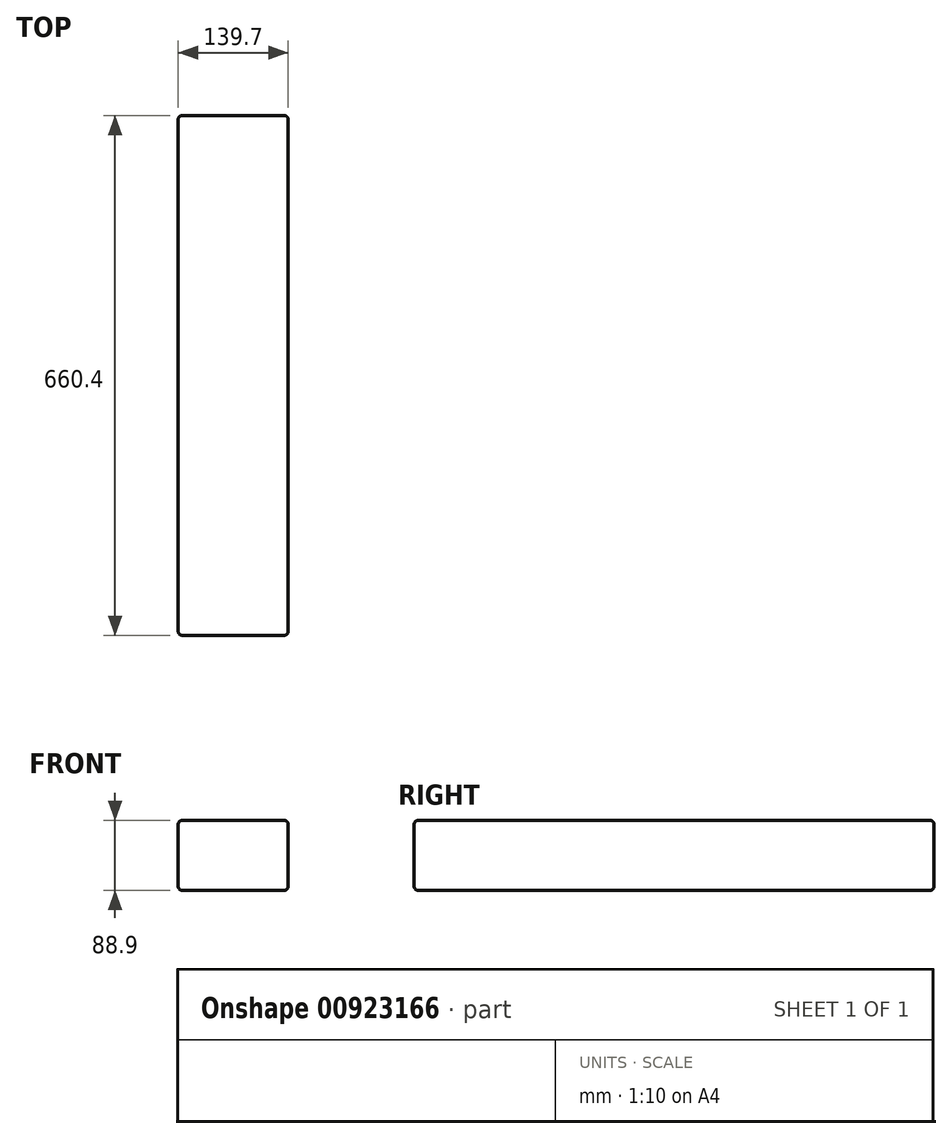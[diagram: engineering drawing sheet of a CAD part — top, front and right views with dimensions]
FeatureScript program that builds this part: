
annotation { "Feature Type Name" : "Feature", "Feature Type Description" : "" }
export const myFeature = defineFeature(function(context is Context, id is Id, definition is map)
    precondition{}
    {
        {
            var Q0;
            Q0=qCreatedBy(makeId("Front.planeOp"),FACE);
            var sketch = newSketch(context, id + "F0", { "sketchPlane" : qUnion([Q0])});
            skLineSegment(sketch, "E0.bottom", {"start": v(-69.85, 44.45) * mm, "end": v(69.85, 44.45) * mm});
            skLineSegment(sketch, "E0.top", {"start": v(-69.85, -44.45) * mm, "end": v(69.85, -44.45) * mm});
            skLineSegment(sketch, "E0.left", {"start": v(-69.85, 44.45) * mm, "end": v(-69.85, -44.45) * mm});
            skLineSegment(sketch, "E0.right", {"start": v(69.85, 44.45) * mm, "end": v(69.85, -44.45) * mm});
            skPoint(sketch, "E0.middle", {"position": v(0, 0) * mm});
            skSolve(sketch);
        }
        {
            var Q0;
            Q0=makeQuery(id+"F0.imprint","IMPRINT",FACE,{"disambiguationData":[TD([[makeQuery(id+"F0.imprint","IMPRINT",EDGE,{"derivedFrom":sQuery(id+"F0.wireOp",EDGE,"E0.bottom")}),-1.0]])]});
            extrude(context, id + "F1", {"entities" : qUnion([Q0]), "endBound" : BoundingType.SYMMETRIC, "depth" : 660.4 * mm, "offsetDistance" : 25.4 * mm});
        }
        {
            var Q0;
            Q0=makeQuery(id+"F1.opExtrude","CAP_EDGE",EDGE,{"disambiguationData":[OSD([sQuery(id+"F0.wireOp",EDGE,"E0.bottom")])],"isStart":false});
            var Q1;
            Q1=makeQuery(id+"F1.opExtrude","CAP_EDGE",EDGE,{"disambiguationData":[OSD([sQuery(id+"F0.wireOp",EDGE,"E0.left")])],"isStart":false});
            var Q2;
            Q2=makeQuery(id+"F1.opExtrude","CAP_EDGE",EDGE,{"disambiguationData":[OSD([sQuery(id+"F0.wireOp",EDGE,"E0.right")])],"isStart":false});
            var Q3;
            Q3=makeQuery(id+"F1.opExtrude","CAP_EDGE",EDGE,{"disambiguationData":[OSD([sQuery(id+"F0.wireOp",EDGE,"E0.top")])],"isStart":false});
            var Q4;
            Q4=makeQuery(id+"F1.opExtrude","SWEPT_EDGE",EDGE,{"disambiguationData":[OSD([sQuery(id+"F0.wireOp",EDGE,"E0.bottom"),sQuery(id+"F0.wireOp",EDGE,"E0.right")])]});
            var Q5;
            Q5=makeQuery(id+"F1.opExtrude","SWEPT_EDGE",EDGE,{"disambiguationData":[OSD([sQuery(id+"F0.wireOp",EDGE,"E0.bottom"),sQuery(id+"F0.wireOp",EDGE,"E0.left")])]});
            var Q6;
            Q6=makeQuery(id+"F1.opExtrude","SWEPT_EDGE",EDGE,{"disambiguationData":[OSD([sQuery(id+"F0.wireOp",EDGE,"E0.top"),sQuery(id+"F0.wireOp",EDGE,"E0.right")])]});
            var Q7;
            Q7=makeQuery(id+"F1.opExtrude","SWEPT_EDGE",EDGE,{"disambiguationData":[OSD([sQuery(id+"F0.wireOp",EDGE,"E0.top"),sQuery(id+"F0.wireOp",EDGE,"E0.left")])]});
            var Q8;
            Q8=makeQuery(id+"F1.opExtrude","CAP_EDGE",EDGE,{"disambiguationData":[OSD([sQuery(id+"F0.wireOp",EDGE,"E0.top")])],"isStart":true});
            var Q9;
            Q9=makeQuery(id+"F1.opExtrude","CAP_EDGE",EDGE,{"disambiguationData":[OSD([sQuery(id+"F0.wireOp",EDGE,"E0.left")])],"isStart":true});
            var Q10;
            Q10=makeQuery(id+"F1.opExtrude","CAP_EDGE",EDGE,{"disambiguationData":[OSD([sQuery(id+"F0.wireOp",EDGE,"E0.bottom")])],"isStart":true});
            var Q11;
            Q11=makeQuery(id+"F1.opExtrude","CAP_EDGE",EDGE,{"disambiguationData":[OSD([sQuery(id+"F0.wireOp",EDGE,"E0.right")])],"isStart":true});
            fillet(context, id + "F2", {"entities" : qUnion([Q0, Q1, Q2, Q3, Q4, Q5, Q6, Q7, Q8, Q9, Q10, Q11]), "radius" : 5.08 * mm, "tangentPropagation" : true, "allowEdgeOverflow" : false});
        }
    });
